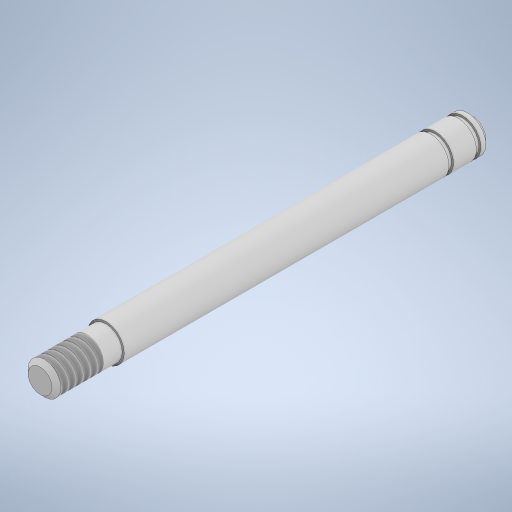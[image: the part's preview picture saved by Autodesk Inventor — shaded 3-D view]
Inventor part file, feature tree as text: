
AUTODESK INVENTOR PART (.ipt)
format: ipt  version: 2024 (Build 280153000, 153)  size: 278,016 bytes
history: native  units: in
note: dims shown in document units (in); Inventor stores cm internally (conversion verified against a paired STEP export)
features: extrude x4, sketch x4, plane x2, chamfer x1, thread x1, direct_edit x1, projected_geometry x1, other x1
ambient origin geometry x8: Origin, YZ Plane, XZ Plane, XY Plane, X Axis, Y Axis, Z Axis, Center Point
bodies: Solid1 (feature_tree)
feature tree (15):
  extrude  "Extrusion1"  Depth=1.25in TaperAngle=0.0deg
  extrude  "Extrusion2"  Depth=0.225in TaperAngle=0.0deg
  plane  "Work Plane1"
  extrude  "Extrusion3"  Depth=0.015in TaperAngle=0.0deg
  plane  "Work Plane2"
  extrude  "Extrusion4"  Depth=0.3937in TaperAngle=0.0deg
  chamfer  "Chamfer1"  Distance=0.015in Angle=45.0deg
  thread  "Thread1"  [1 undecoded]
  direct_edit  "Direct Edit1"
  sketch  "Sketch1"  dims[d0=0.125in d1=1.25in d2=0.0in]
  sketch  "Sketch2"  dims[d3=0.112in d4=0.225in d5=0.0in]
  sketch  "Sketch3"  dims[d6=-0.032in d7=0.015in d8=0.0in]
  projected_geometry  "Projected Loop1"
  sketch  "Sketch4"  dims[d9=-0.0938in d10=0.015in d11=0.0in d12=0.015in d13=0.125in d14=45.0deg d15=0.315in d16=0.0in d17=3.937in d18=0.3937in d19=0.3937in]
  other  "Scale1"
note: 1 required parameter value undecoded (feature->parameter linkage not recoverable at this tier; creation-order binding heuristic only, values carry confidence <= 0.55)
